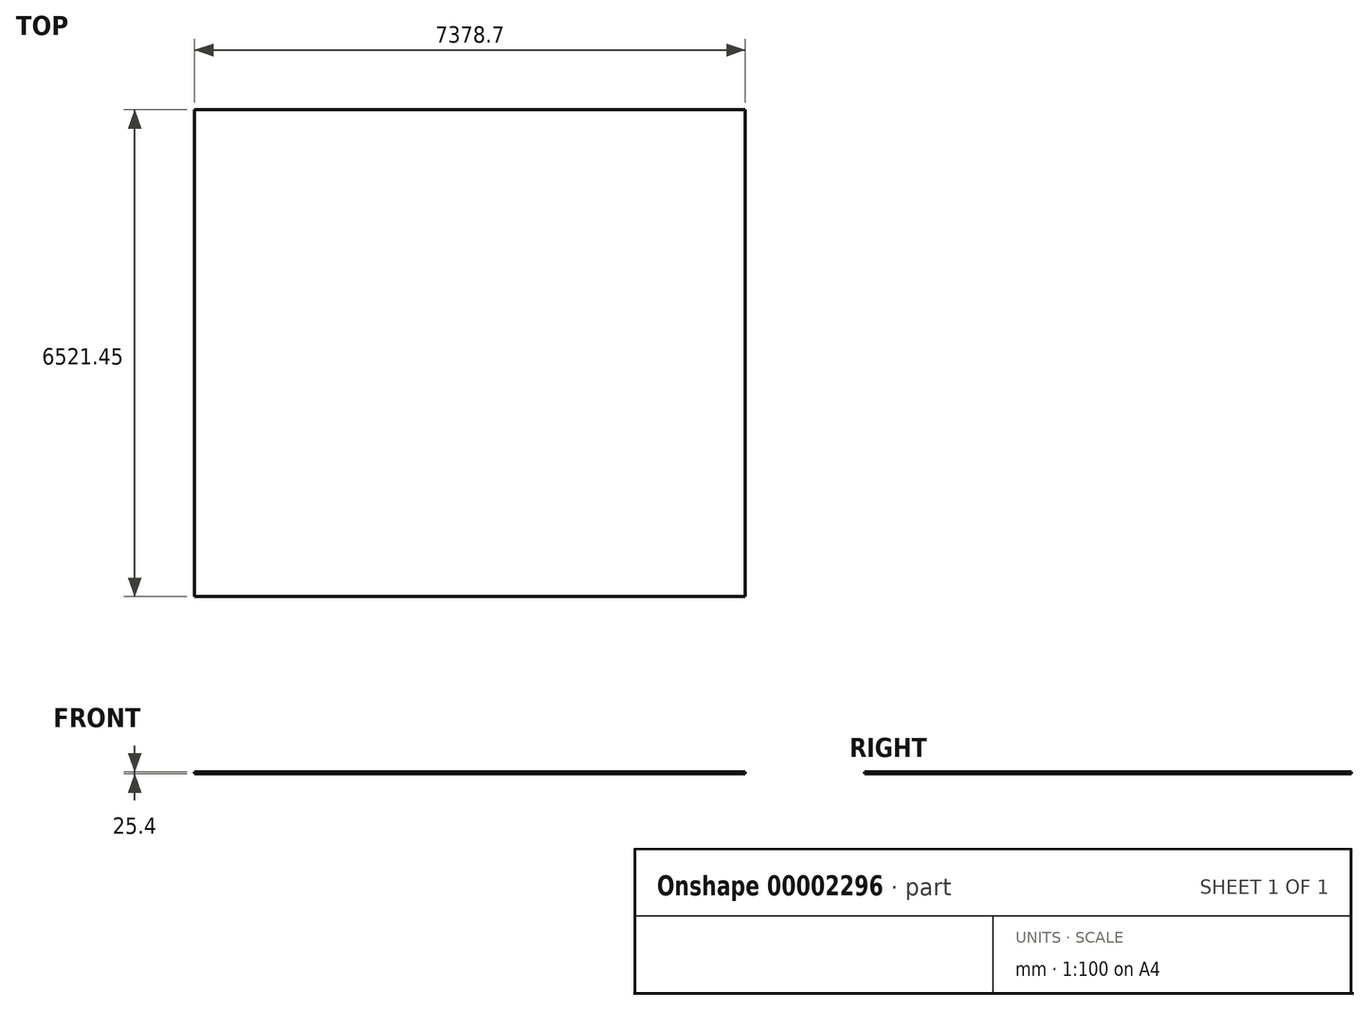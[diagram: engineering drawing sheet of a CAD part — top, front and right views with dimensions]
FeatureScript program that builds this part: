
annotation { "Feature Type Name" : "Feature", "Feature Type Description" : "" }
export const myFeature = defineFeature(function(context is Context, id is Id, definition is map)
    precondition{}
    {
        {
            var Q0;
            Q0=qCreatedBy(makeId("Top.planeOp"),FACE);
            var sketch = newSketch(context, id + "F0", { "sketchPlane" : qUnion([Q0])});
            skLineSegment(sketch, "E0.bottom", {"start": v(0, 0) * mm, "end": v(7378.7, 0) * mm});
            skLineSegment(sketch, "E0.top", {"start": v(0, 6521.45) * mm, "end": v(7378.7, 6521.45) * mm});
            skLineSegment(sketch, "E0.left", {"start": v(0, 0) * mm, "end": v(0, 6521.45) * mm});
            skLineSegment(sketch, "E0.right", {"start": v(7378.7, 0) * mm, "end": v(7378.7, 6521.45) * mm});
            skSolve(sketch);
        }
        {
            var Q0;
            Q0 = qSketchRegion(id + "F0", true);
            extrude(context, id + "F1", {"entities" : qUnion([Q0]), "depth" : 25.4 * mm});
        }
    });
